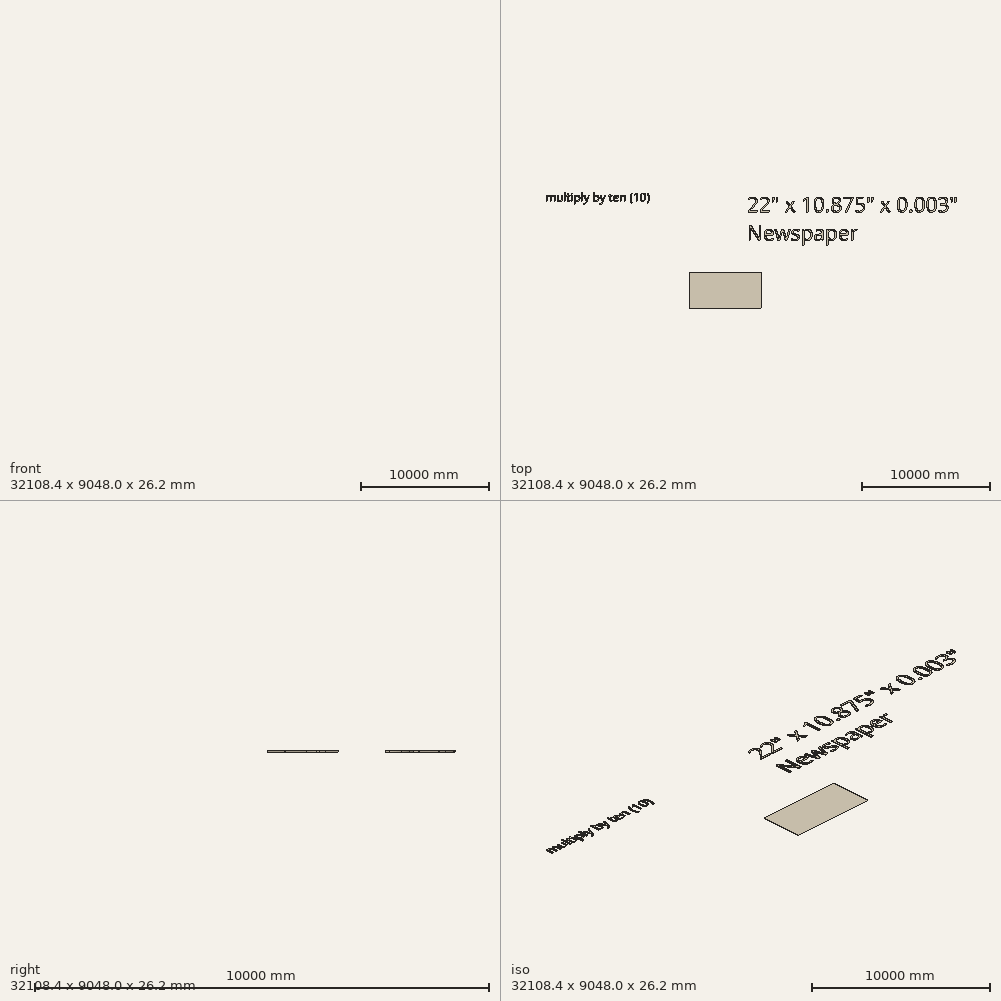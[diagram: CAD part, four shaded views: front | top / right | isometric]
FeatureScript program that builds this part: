
annotation { "Feature Type Name" : "Feature", "Feature Type Description" : "" }
export const myFeature = defineFeature(function(context is Context, id is Id, definition is map)
    precondition{}
    {
        {
            var Q0;
            Q0=qCreatedBy(makeId("Top.planeOp"),FACE);
            var sketch = newSketch(context, id + "F0", { "sketchPlane" : qUnion([Q0])});
            skLineSegment(sketch, "E0.bottom", {"start": v(5034, -4265.23) * mm, "end": v(-554, -4265.23) * mm});
            skLineSegment(sketch, "E0.top", {"start": v(5034, -7027.48) * mm, "end": v(-554, -7027.48) * mm});
            skLineSegment(sketch, "E0.left", {"start": v(5034, -4265.23) * mm, "end": v(5034, -7027.48) * mm});
            skLineSegment(sketch, "E0.right", {"start": v(-554, -4265.23) * mm, "end": v(-554, -7027.48) * mm});
            skPoint(sketch, "E0.middle", {"position": v(2240, -5646.35) * mm});
            skSolve(sketch);
        }
        {
            var Q0;
            Q0 = qSketchRegion(id + "F0", true);
            extrude(context, id + "F1", {"entities" : qUnion([Q0]), "depth" : 0.76 * mm});
        }
        {
            var Q0;
            Q0=makeQuery(id+"F1.opExtrude","CAP_FACE",FACE,{"disambiguationData":[OSD([sQuery(id+"F0.wireOp",EDGE,"E0.bottom"),sQuery(id+"F0.wireOp",EDGE,"E0.top"),sQuery(id+"F0.wireOp",EDGE,"E0.left"),sQuery(id+"F0.wireOp",EDGE,"E0.right")])],"isStart":false});
            var sketch = newSketch(context, id + "F2", { "sketchPlane" : qUnion([Q0])});
            skText(sketch, "E1", { "text": "22\" x 10.875\" x 0.003\"\nNewspaper", "fontName": "OpenSans-Regular.ttf"});
            const initialGuessF2  = {"E1": [3.938, 0.49028, 1, 0, 1.17481]};
            skSetInitialGuess(sketch, initialGuessF2);
            skSolve(sketch);
        }
        {
            var Q0;
            Q0 = qSketchRegion(id + "F2", true);
            extrude(context, id + "F3", {"entities" : qUnion([Q0]), "depth" : 25.4 * mm});
        }
        {
            var Q0;
            Q0=qCreatedBy(makeId("Top.planeOp"),FACE);
            var sketch = newSketch(context, id + "F4", { "sketchPlane" : qUnion([Q0])});
            skText(sketch, "E2", { "text": "multiply by ten (10)", "fontName": "OpenSans-Regular.ttf"});
            const initialGuessF4  = {"E2": [-11.85706, 1.3245, 1, 0, 0.65954]};
            skSetInitialGuess(sketch, initialGuessF4);
            skSolve(sketch);
        }
        {
            var Q0;
            Q0 = qSketchRegion(id + "F4", true);
            extrude(context, id + "F5", {"entities" : qUnion([Q0]), "depth" : 25.4 * mm});
        }
    });
